# Revit family: Legolite Commercial Downlight 263007
name_source: partatom
category: Lighting Fixtures
units: mm (PartAtom-declared; Revit-internal decimal feet)

## family parameters
Always vertical = Yes
Cut with Voids When Loaded = No
Host = Ceiling
Light Source = Yes
OmniClass Number = 23.80.00.00
OmniClass Title = Electric Power and Lighting
Part Type = Normal
Room Calculation Point = No
Round Connector Dimension = Use Diameter
Shared = No

## types (6) — shared parameters
Color Filter = 16777215
Data Sheet = 211024.pdf
Description = Stellar V Pro Five-CCT LED Batten 4FT 40W(10/14/20/24/26/30/36/40W) 3000K/4000K/5000K/5700K/6500K CCT Selectable 125lm/W Non-Dim IP20 Width:80mm
Dimming Lamp Color Temperature Shift = <None>
Emit Shape Visible in Rendering = No
Emit from Circle Diameter = 215 mm
Height = 71 mm  [stored 0.23294 ft]
Lamp = Legolite Commercial Downlight 263007
Length = 1200 mm  [stored 3.93701 ft]
Manufacturer = Energetic Lighting
Material (Body) = <By Category>
Material (Diffuser) = <By Category>
Model = YKT8BG2-FC-N-2L120 40W
Tilt Angle = 90.00°
Type Comments = CCT Selectable, Non-Dim IP20
Width = 80 mm  [stored 0.262467 ft]
zero-valued in all types: Default Elevation

## per-type parameters (varying)
| type | Photometric Web File |
| 12W 3000K | 263007 12W 3000K.ies |
| 12W 4000K | 263007 12W 4000K.ies |
| 12W 5000K | 263007 12W 5000K.ies |
| 8W 3000K | 263007 8W 3000K.ies |
| 8W 4000K | 263007 8W 4000K.ies |
| 8W 5000K | 263007 8W 5000K.ies |

note: [stored X ft] marks values corroborated as IEEE doubles in the binary element streams (Revit-internal decimal feet)

## geometry (parser evidence)
native form markers: Sweep x3
no freeform markers — native parametric forms only
